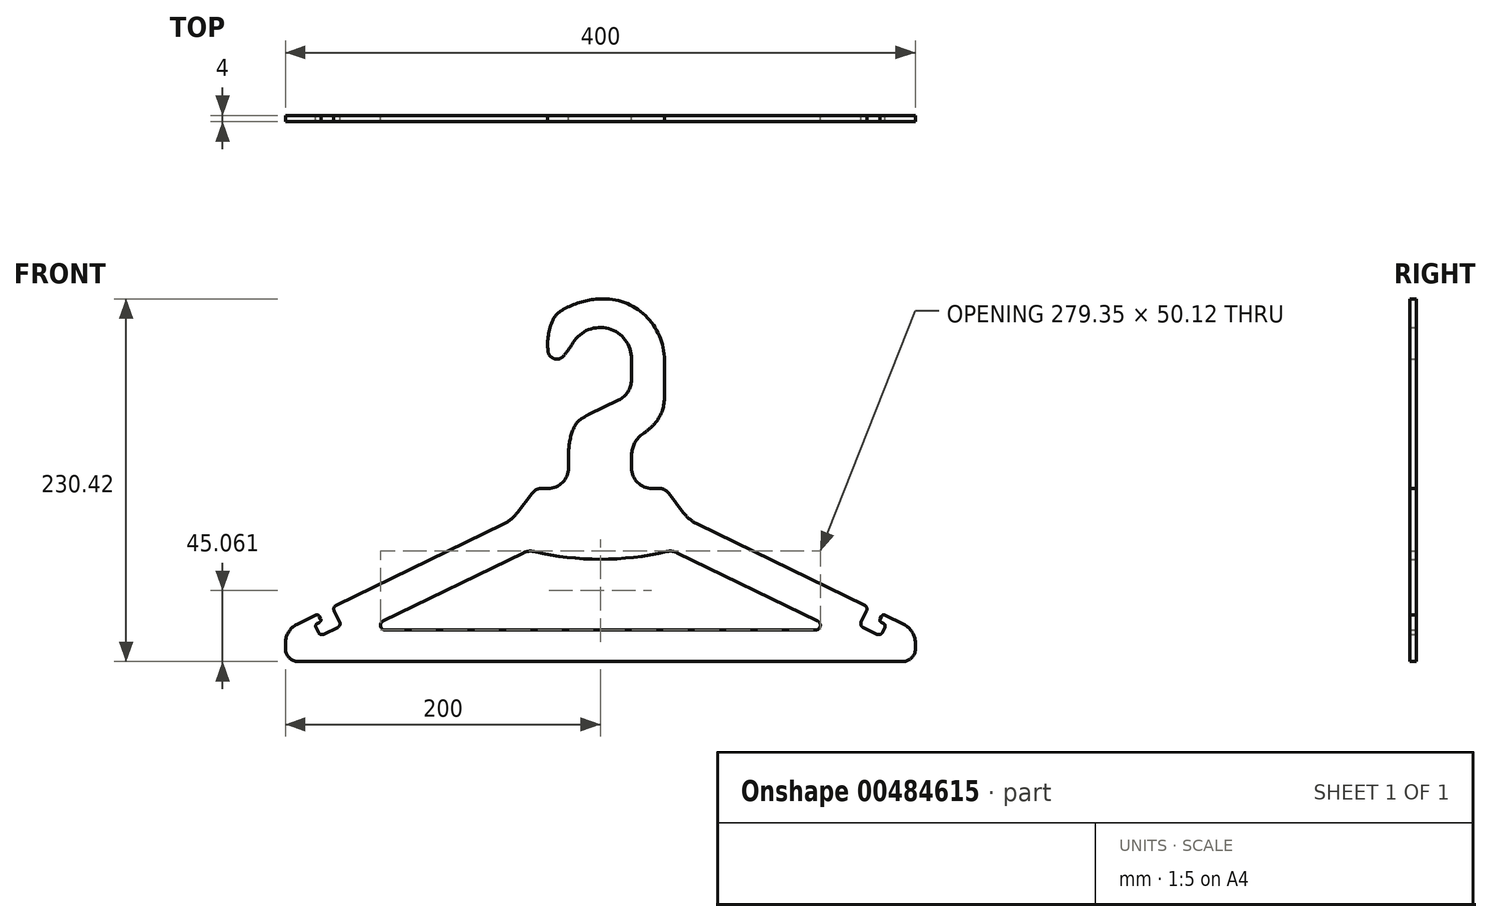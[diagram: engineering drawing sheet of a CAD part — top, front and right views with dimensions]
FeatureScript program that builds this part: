
annotation { "Feature Type Name" : "Feature", "Feature Type Description" : "" }
export const myFeature = defineFeature(function(context is Context, id is Id, definition is map)
    precondition{}
    {
        {
            var Q0;
            Q0=qCreatedBy(makeId("Front.planeOp"),FACE);
            var sketch = newSketch(context, id + "F0", { "sketchPlane" : qUnion([Q0])});
            skLineSegment(sketch, "E0", {"start": v(0, 0) * mm, "end": v(0, 266.9) * mm, "construction": true});
            skLineSegment(sketch, "E1", {"start": v(0, 0) * mm, "end": v(0, -107.96) * mm, "construction": true});
            skSolve(sketch);
        }
        {
            var Q0;
            Q0=qCreatedBy(makeId("Front.planeOp"),FACE);
            var sketch = newSketch(context, id + "F1", { "sketchPlane" : qUnion([Q0])});
            skLineSegment(sketch, "E2", {"start": v(0, 0) * mm, "end": v(-192, 0) * mm});
            skLineSegment(sketch, "E3", {"start": v(-200, 8) * mm, "end": v(-200, 11.87) * mm});
            skLineSegment(sketch, "E4", {"start": v(-192.69, 23.56) * mm, "end": v(-180.55, 29.46) * mm});
            skLineSegment(sketch, "E5", {"start": v(-52.5, 94.84) * mm, "end": v(-43.53, 106.8) * mm});
            skLineSegment(sketch, "E6", {"start": v(-37.13, 110) * mm, "end": v(0, 110) * mm});
            skPoint(sketch, "E7.visualSharp", {"position": v(-56.13, 90) * mm});
            skArc(sketch, "E7.filletArc", {"start": v(-61.56, 87.36) * mm, "mid": v(-56.58, 90.56) * mm, "end": v(-52.5, 94.84) * mm});
            skPoint(sketch, "E8.visualSharp", {"position": v(-41.13, 110) * mm});
            skArc(sketch, "E8.filletArc", {"start": v(-37.13, 110) * mm, "mid": v(-40.7, 109.16) * mm, "end": v(-43.53, 106.8) * mm});
            skPoint(sketch, "E9.visualSharp", {"position": v(-200, 20) * mm});
            skArc(sketch, "E9.filletArc", {"start": v(-192.69, 23.56) * mm, "mid": v(-198.02, 18.76) * mm, "end": v(-200, 11.87) * mm});
            skLineSegment(sketch, "E10.trimOffspring", {"start": v(-167.96, 35.59) * mm, "end": v(-61.56, 87.36) * mm});
            skPoint(sketch, "E11.visualSharp", {"position": v(-200, 0) * mm});
            skArc(sketch, "E11.filletArc", {"start": v(-200, 8) * mm, "mid": v(-197.66, 2.34) * mm, "end": v(-192, 0) * mm});
            skPoint(sketch, "E12.visualSharp", {"position": v(-164.03, 37.5) * mm});
            skPoint(sketch, "E13.visualSharp", {"position": v(-183.82, 27.87) * mm});
            skPoint(sketch, "E14.orphan", {"position": v(-159.53, 39.69) * mm});
            skPoint(sketch, "E15.orphan", {"position": v(-189.15, 25.28) * mm});
            skLineSegment(sketch, "E16", {"start": v(-169.11, 32.25) * mm, "end": v(-165.61, 25.05) * mm});
            skLineSegment(sketch, "E17", {"start": v(-166.77, 21.71) * mm, "end": v(-175.76, 17.34) * mm});
            skLineSegment(sketch, "E18", {"start": v(-179.1, 18.5) * mm, "end": v(-180.63, 21.64) * mm});
            skLineSegment(sketch, "E19", {"start": v(-179.7, 24.31) * mm, "end": v(-178.36, 24.97) * mm});
            skLineSegment(sketch, "E20", {"start": v(-177.67, 26.97) * mm, "end": v(-178.54, 28.77) * mm});
            skPoint(sketch, "E21.visualSharp", {"position": v(-179.2, 30.12) * mm});
            skArc(sketch, "E21.filletArc", {"start": v(-178.54, 28.77) * mm, "mid": v(-179.4, 29.53) * mm, "end": v(-180.55, 29.46) * mm});
            skPoint(sketch, "E22.visualSharp", {"position": v(-177.01, 25.62) * mm});
            skArc(sketch, "E22.filletArc", {"start": v(-178.36, 24.97) * mm, "mid": v(-177.6, 25.83) * mm, "end": v(-177.67, 26.97) * mm});
            skPoint(sketch, "E23.visualSharp", {"position": v(-181.5, 23.44) * mm});
            skArc(sketch, "E23.filletArc", {"start": v(-179.7, 24.31) * mm, "mid": v(-180.72, 23.17) * mm, "end": v(-180.63, 21.64) * mm});
            skPoint(sketch, "E24.visualSharp", {"position": v(-178, 16.24) * mm});
            skArc(sketch, "E24.filletArc", {"start": v(-179.1, 18.5) * mm, "mid": v(-177.67, 17.22) * mm, "end": v(-175.76, 17.34) * mm});
            skPoint(sketch, "E25.visualSharp", {"position": v(-170.2, 34.5) * mm});
            skArc(sketch, "E25.filletArc", {"start": v(-167.96, 35.59) * mm, "mid": v(-169.23, 34.16) * mm, "end": v(-169.11, 32.25) * mm});
            skPoint(sketch, "E26.visualSharp", {"position": v(-164.52, 22.8) * mm});
            skArc(sketch, "E26.filletArc", {"start": v(-166.77, 21.71) * mm, "mid": v(-165.5, 23.14) * mm, "end": v(-165.61, 25.05) * mm});
            skArc(sketch, "E27.MirrorCS", {"start": v(179.7, 24.31) * mm, "mid": v(180.72, 23.17) * mm, "end": v(180.63, 21.64) * mm});
            skLineSegment(sketch, "E28.MirrorCS", {"start": v(179.1, 18.5) * mm, "end": v(180.63, 21.64) * mm});
            skArc(sketch, "E29.MirrorCS", {"start": v(178.36, 24.97) * mm, "mid": v(177.6, 25.83) * mm, "end": v(177.67, 26.97) * mm});
            skLineSegment(sketch, "E30.MirrorCS", {"start": v(179.7, 24.31) * mm, "end": v(178.36, 24.97) * mm});
            skLineSegment(sketch, "E31.MirrorCS", {"start": v(177.67, 26.97) * mm, "end": v(178.54, 28.77) * mm});
            skArc(sketch, "E32.MirrorCS", {"start": v(178.54, 28.77) * mm, "mid": v(179.4, 29.53) * mm, "end": v(180.55, 29.46) * mm});
            skArc(sketch, "E33.MirrorCS", {"start": v(179.1, 18.5) * mm, "mid": v(177.67, 17.22) * mm, "end": v(175.76, 17.34) * mm});
            skLineSegment(sketch, "E34.MirrorCS", {"start": v(166.77, 21.71) * mm, "end": v(175.76, 17.34) * mm});
            skArc(sketch, "E35.MirrorCS", {"start": v(166.77, 21.71) * mm, "mid": v(165.5, 23.14) * mm, "end": v(165.61, 25.05) * mm});
            skArc(sketch, "E36.MirrorCS", {"start": v(167.96, 35.59) * mm, "mid": v(169.23, 34.16) * mm, "end": v(169.11, 32.25) * mm});
            skLineSegment(sketch, "E37.MirrorCS", {"start": v(192.69, 23.56) * mm, "end": v(180.55, 29.46) * mm});
            skArc(sketch, "E38.MirrorCS", {"start": v(192.69, 23.56) * mm, "mid": v(198.02, 18.76) * mm, "end": v(200, 11.87) * mm});
            skArc(sketch, "E39.MirrorCS", {"start": v(37.13, 110) * mm, "mid": v(40.7, 109.16) * mm, "end": v(43.53, 106.8) * mm});
            skLineSegment(sketch, "E40.MirrorCS", {"start": v(169.11, 32.25) * mm, "end": v(165.61, 25.05) * mm});
            skLineSegment(sketch, "E41.MirrorCS", {"start": v(200, 8) * mm, "end": v(200, 11.87) * mm});
            skArc(sketch, "E42.MirrorCS", {"start": v(61.56, 87.36) * mm, "mid": v(56.58, 90.56) * mm, "end": v(52.5, 94.84) * mm});
            skArc(sketch, "E43.MirrorCS", {"start": v(200, 8) * mm, "mid": v(197.66, 2.34) * mm, "end": v(192, 0) * mm});
            skLineSegment(sketch, "E44.MirrorCS", {"start": v(52.5, 94.84) * mm, "end": v(43.53, 106.8) * mm});
            skPoint(sketch, "E45.MirrorP", {"position": v(181.5, 23.44) * mm});
            skPoint(sketch, "E46.MirrorP", {"position": v(179.2, 30.12) * mm});
            skPoint(sketch, "E47.MirrorP", {"position": v(177.01, 25.62) * mm});
            skPoint(sketch, "E48.MirrorP", {"position": v(56.13, 90) * mm});
            skPoint(sketch, "E49.MirrorP", {"position": v(164.03, 37.5) * mm});
            skLineSegment(sketch, "E50.MirrorCS", {"start": v(37.13, 110) * mm, "end": v(0, 110) * mm});
            skPoint(sketch, "E51.MirrorP", {"position": v(159.53, 39.69) * mm});
            skPoint(sketch, "E52.MirrorP", {"position": v(200, 0) * mm});
            skPoint(sketch, "E53.MirrorP", {"position": v(183.82, 27.87) * mm});
            skPoint(sketch, "E54.MirrorP", {"position": v(178, 16.24) * mm});
            skPoint(sketch, "E55.MirrorP", {"position": v(200, 20) * mm});
            skLineSegment(sketch, "E56.MirrorCS", {"start": v(167.96, 35.59) * mm, "end": v(61.56, 87.36) * mm});
            skLineSegment(sketch, "E57.MirrorCS", {"start": v(0, 0) * mm, "end": v(192, 0) * mm});
            skPoint(sketch, "E58.MirrorP", {"position": v(189.15, 25.28) * mm});
            skPoint(sketch, "E59.MirrorP", {"position": v(164.52, 22.8) * mm});
            skPoint(sketch, "E60.MirrorP", {"position": v(170.2, 34.5) * mm});
            skPoint(sketch, "E61.MirrorP", {"position": v(41.13, 110) * mm});
            skSolve(sketch);
        }
        {
            var Q0;
            Q0=qCreatedBy(makeId("Front.planeOp"),FACE);
            var sketch = newSketch(context, id + "F2", { "sketchPlane" : qUnion([Q0])});
            skLineSegment(sketch, "E62.0", {"start": v(-138, 25.7) * mm, "end": v(-48.76, 69.12) * mm});
            skLineSegment(sketch, "E63.0", {"start": v(0, 20) * mm, "end": v(-136.7, 20) * mm});
            skLineSegment(sketch, "E64", {"start": v(-25.94, 65) * mm, "end": v(21.34, 65) * mm, "construction": true});
            skArc(sketch, "E65", {"start": v(-42.1, 69.86) * mm, "mid": v(-21.2, 66.22) * mm, "end": v(0, 65) * mm});
            skPoint(sketch, "E66.visualSharp", {"position": v(-45.52, 70.7) * mm});
            skArc(sketch, "E66.filletArc", {"start": v(-42.1, 69.86) * mm, "mid": v(-45.5, 70.06) * mm, "end": v(-48.76, 69.12) * mm});
            skPoint(sketch, "E67.visualSharp", {"position": v(-149.71, 20) * mm});
            skArc(sketch, "E67.filletArc", {"start": v(-138, 25.7) * mm, "mid": v(-139.61, 22.33) * mm, "end": v(-136.7, 20) * mm});
            skArc(sketch, "E68.MirrorCS", {"start": v(138, 25.7) * mm, "mid": v(139.61, 22.33) * mm, "end": v(136.7, 20) * mm});
            skArc(sketch, "E69.MirrorCS", {"start": v(42.1, 69.86) * mm, "mid": v(45.5, 70.06) * mm, "end": v(48.76, 69.12) * mm});
            skPoint(sketch, "E70.MirrorP", {"position": v(149.71, 20) * mm});
            skPoint(sketch, "E71.MirrorP", {"position": v(45.52, 70.7) * mm});
            skLineSegment(sketch, "E72.MirrorCS", {"start": v(138, 25.7) * mm, "end": v(48.76, 69.12) * mm});
            skArc(sketch, "E73.MirrorCS", {"start": v(42.1, 69.86) * mm, "mid": v(21.2, 66.22) * mm, "end": v(0, 65) * mm});
            skLineSegment(sketch, "E74.MirrorCS", {"start": v(0, 20) * mm, "end": v(136.7, 20) * mm});
            skSolve(sketch);
        }
        {
            var Q0;
            Q0=qCreatedBy(makeId("Front.planeOp"),FACE);
            var sketch = newSketch(context, id + "F3", { "sketchPlane" : qUnion([Q0])});
            skPoint(sketch, "E75.0", {"position": v(-0.2, 110) * mm});
            skLineSegment(sketch, "E76.0", {"start": v(-35.32, 110) * mm, "end": v(-33.2, 110) * mm});
            skLineSegment(sketch, "E76.1", {"start": v(34.93, 110) * mm, "end": v(32.8, 110) * mm});
            skLineSegment(sketch, "E77", {"start": v(19.8, 123) * mm, "end": v(19.8, 131) * mm});
            skCircle(sketch, "E78", {"center": v(-0.2, 192.12) * mm, "radius": 20 * mm, "construction": true});
            skLineSegment(sketch, "E79", {"start": v(-7.5, 156.77) * mm, "end": v(11.55, 166.04) * mm});
            skArc(sketch, "E80", {"start": v(-7.5, 156.77) * mm, "mid": v(-9.89, 155.5) * mm, "end": v(-12.2, 154.08) * mm});
            skArc(sketch, "E81", {"start": v(-12.2, 154.08) * mm, "mid": v(-14.85, 151.72) * mm, "end": v(-16.74, 148.72) * mm});
            skArc(sketch, "E82", {"start": v(-16.74, 148.72) * mm, "mid": v(-19.33, 140.81) * mm, "end": v(-20.2, 132.54) * mm});
            skLineSegment(sketch, "E83", {"start": v(-20.2, 123) * mm, "end": v(-20.2, 132.54) * mm});
            skArc(sketch, "E84", {"start": v(34.37, 151.04) * mm, "mid": v(31.01, 147.75) * mm, "end": v(27.27, 144.9) * mm});
            skArc(sketch, "E85", {"start": v(27.27, 144.9) * mm, "mid": v(21.79, 138.9) * mm, "end": v(19.8, 131) * mm});
            skArc(sketch, "E86", {"start": v(11.55, 166.04) * mm, "mid": v(17.44, 171.3) * mm, "end": v(19.69, 178.86) * mm});
            skLineSegment(sketch, "E87", {"start": v(19.69, 178.86) * mm, "end": v(19.86, 192.12) * mm});
            skArc(sketch, "E88", {"start": v(19.86, 192.12) * mm, "mid": v(5.23, 211.42) * mm, "end": v(-17.3, 202.56) * mm});
            skArc(sketch, "E89", {"start": v(-33.3, 197.14) * mm, "mid": v(-29.37, 192.34) * mm, "end": v(-23.42, 194.08) * mm});
            skArc(sketch, "E90", {"start": v(-23.42, 194.08) * mm, "mid": v(-20.2, 198.2) * mm, "end": v(-17.3, 202.56) * mm});
            skArc(sketch, "E91", {"start": v(-20.88, 225.06) * mm, "mid": v(-23.28, 223.79) * mm, "end": v(-25.59, 222.37) * mm});
            skArc(sketch, "E92", {"start": v(-25.59, 222.37) * mm, "mid": v(-28.27, 219.97) * mm, "end": v(-30.18, 216.9) * mm});
            skArc(sketch, "E93", {"start": v(-30.18, 216.9) * mm, "mid": v(-33.01, 207.22) * mm, "end": v(-33.3, 197.14) * mm});
            skArc(sketch, "E94", {"start": v(-20.88, 225.06) * mm, "mid": v(-10.8, 228.76) * mm, "end": v(-0.2, 230.37) * mm});
            skArc(sketch, "E95", {"start": v(-0.2, 230.37) * mm, "mid": v(28.56, 219.7) * mm, "end": v(40.65, 191.52) * mm});
            skLineSegment(sketch, "E96", {"start": v(40.65, 167.38) * mm, "end": v(40.65, 191.52) * mm});
            skArc(sketch, "E97.filletArc", {"start": v(-33.2, 110) * mm, "mid": v(-24, 113.8) * mm, "end": v(-20.2, 123) * mm});
            skArc(sketch, "E98.filletArc", {"start": v(19.8, 123) * mm, "mid": v(23.62, 113.8) * mm, "end": v(32.8, 110) * mm});
            skArc(sketch, "E99", {"start": v(34.37, 151.04) * mm, "mid": v(39.02, 158.63) * mm, "end": v(40.65, 167.38) * mm});
            skLineSegment(sketch, "E100", {"start": v(-33.2, 110) * mm, "end": v(32.8, 110) * mm});
            skSolve(sketch);
        }
        {
            var Q0;
            Q0=qSketchRegion(id+"F1",true);
            extrude(context, id + "F4", {"entities" : qUnion([Q0]), "depth" : 4 * mm, "offsetDistance" : 25 * mm});
        }
        {
            var Q0;
            Q0=qSketchRegion(id+"F2",true);
            extrude(context, id + "F5", {"entities" : qUnion([Q0]), "operationType" : NewBodyOperationType.REMOVE, "depth" : 25 * mm, "offsetDistance" : 25 * mm});
        }
        {
            var Q0;
            Q0=qSketchRegion(id+"F3",true);
            extrude(context, id + "F6", {"entities" : qUnion([Q0]), "operationType" : NewBodyOperationType.ADD, "depth" : 4 * mm, "offsetDistance" : 25 * mm});
        }
    });
